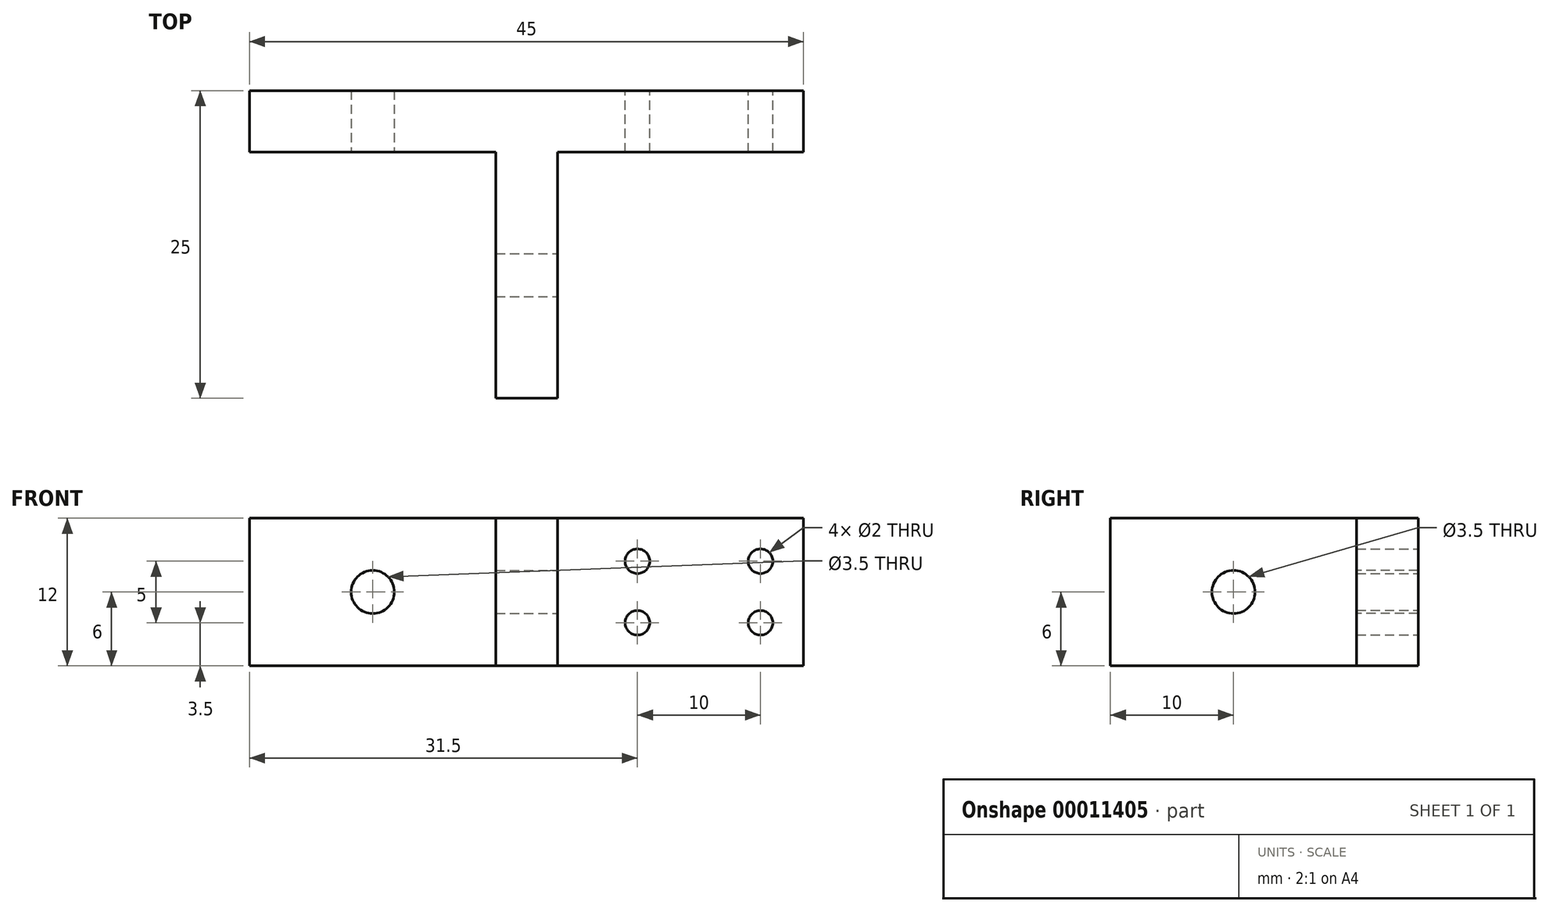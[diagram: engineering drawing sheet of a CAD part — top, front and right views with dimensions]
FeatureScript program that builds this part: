
annotation { "Feature Type Name" : "Feature", "Feature Type Description" : "" }
export const myFeature = defineFeature(function(context is Context, id is Id, definition is map)
    precondition{}
    {
        {
            var Q0;
            Q0=qCreatedBy(makeId("Top.planeOp"),FACE);
            var sketch = newSketch(context, id + "F0", { "sketchPlane" : qUnion([Q0])});
            skLineSegment(sketch, "E0.bottom", {"start": v(20, 0) * mm, "end": v(25, 0) * mm});
            skLineSegment(sketch, "E0.top", {"start": v(0, 25) * mm, "end": v(25, 25) * mm});
            skLineSegment(sketch, "E0.left", {"start": v(0, 20) * mm, "end": v(0, 25) * mm});
            skLineSegment(sketch, "E0.right", {"start": v(25, 0) * mm, "end": v(25, 20) * mm});
            skLineSegment(sketch, "E1.top", {"start": v(0, 20) * mm, "end": v(20, 20) * mm});
            skLineSegment(sketch, "E1.right", {"start": v(20, 0) * mm, "end": v(20, 20) * mm});
            skLineSegment(sketch, "E2.bottom", {"start": v(25, 25) * mm, "end": v(45, 25) * mm});
            skLineSegment(sketch, "E2.top", {"start": v(25, 20) * mm, "end": v(45, 20) * mm});
            skLineSegment(sketch, "E2.right", {"start": v(45, 25) * mm, "end": v(45, 20) * mm});
            skSolve(sketch);
        }
        {
            var Q0;
            Q0=makeQuery(id+"F0.imprint","IMPRINT",FACE,{"disambiguationData":[TD([[makeQuery(id+"F0.imprint","IMPRINT",EDGE,{"derivedFrom":sQuery(id+"F0.wireOp",EDGE,"E0.bottom")}),1.0]])]});
            extrude(context, id + "F1", {"entities" : qUnion([Q0]), "depth" : 12 * mm});
        }
        {
            var Q0;
            Q0=makeQuery(id+"F1.opExtrude","SWEPT_FACE",FACE,{"disambiguationData":[OSD([sQuery(id+"F0.wireOp",EDGE,"E0.right")])]});
            var sketch = newSketch(context, id + "F2", { "sketchPlane" : qUnion([Q0])});
            skCircle(sketch, "E3", {"center": v(10, 6) * mm, "radius": 1.75 * mm});
            skPoint(sketch, "E4.orphan", {"position": v(0, 0) * mm});
            skPoint(sketch, "E5.orphan", {"position": v(20, 12) * mm});
            skSolve(sketch);
        }
        {
            var Q0;
            Q0=makeQuery(id+"F2.imprint","IMPRINT",FACE,{"disambiguationData":[TD([[makeQuery(id+"F2.imprint","IMPRINT",EDGE,{"derivedFrom":sQuery(id+"F2.wireOp",EDGE,"E3")}),1.0]])]});
            var Q1;
            Q1=sQuery(id+"F2.wireOp",EDGE,"E3");
            extrude(context, id + "F3", {"entities" : qUnion([Q0]), "operationType" : NewBodyOperationType.REMOVE, "surfaceEntities" : qUnion([Q1]), "oppositeDirection" : true, "depth" : 5 * mm});
        }
        {
            var Q0;
            Q0=makeQuery(id+"F1.opExtrude","SWEPT_FACE",FACE,{"disambiguationData":[OSD([sQuery(id+"F0.wireOp",EDGE,"E1.top")])]});
            var sketch = newSketch(context, id + "F4", { "sketchPlane" : qUnion([Q0])});
            skCircle(sketch, "E6", {"center": v(10, 6) * mm, "radius": 1.75 * mm});
            skPoint(sketch, "E7.orphan", {"position": v(0, 12) * mm});
            skPoint(sketch, "E8.orphan", {"position": v(20, 0) * mm});
            skSolve(sketch);
        }
        {
            var Q0;
            Q0 = qSketchRegion(id + "F4", true);
            extrude(context, id + "F5", {"entities" : qUnion([Q0]), "operationType" : NewBodyOperationType.REMOVE, "oppositeDirection" : true, "depth" : 5 * mm});
        }
        {
            var Q0;
            Q0=makeQuery(id+"F1.opExtrude","SWEPT_FACE",FACE,{"disambiguationData":[OSD([sQuery(id+"F0.wireOp",EDGE,"E0.top"),sQuery(id+"F0.wireOp",EDGE,"E2.bottom")])]});
            var sketch = newSketch(context, id + "F6", { "sketchPlane" : qUnion([Q0])});
            skLineSegment(sketch, "E9.bottom", {"start": v(-45, 0) * mm, "end": v(-41.5, 0) * mm});
            skLineSegment(sketch, "E9.left", {"start": v(-45, 0) * mm, "end": v(-45, 3.5) * mm});
            skLineSegment(sketch, "E10.bottom", {"start": v(-45, 12) * mm, "end": v(-41.5, 12) * mm});
            skLineSegment(sketch, "E10.left", {"start": v(-45, 12) * mm, "end": v(-45, 8.5) * mm});
            skLineSegment(sketch, "E11.bottom", {"start": v(-41.5, 0) * mm, "end": v(-31.5, 0) * mm});
            skLineSegment(sketch, "E12.bottom", {"start": v(-41.5, 12) * mm, "end": v(-31.5, 12) * mm});
            skCircle(sketch, "E13", {"center": v(-41.5, 3.5) * mm, "radius": 1 * mm});
            skCircle(sketch, "E14", {"center": v(-31.5, 3.5) * mm, "radius": 1 * mm});
            skCircle(sketch, "E15", {"center": v(-31.5, 8.5) * mm, "radius": 1 * mm});
            skCircle(sketch, "E16", {"center": v(-41.5, 8.5) * mm, "radius": 1 * mm});
            skSolve(sketch);
        }
        {
            var Q0;
            Q0=makeQuery(id+"F6.imprint","IMPRINT",FACE,{"disambiguationData":[TD([[makeQuery(id+"F6.imprint","IMPRINT",EDGE,{"derivedFrom":sQuery(id+"F6.wireOp",EDGE,"E16")}),1.0]])]});
            var Q1;
            Q1=makeQuery(id+"F6.imprint","IMPRINT",FACE,{"disambiguationData":[TD([[makeQuery(id+"F6.imprint","IMPRINT",EDGE,{"derivedFrom":sQuery(id+"F6.wireOp",EDGE,"E15")}),1.0]])]});
            var Q2;
            Q2=makeQuery(id+"F6.imprint","IMPRINT",FACE,{"disambiguationData":[TD([[makeQuery(id+"F6.imprint","IMPRINT",EDGE,{"derivedFrom":sQuery(id+"F6.wireOp",EDGE,"E14")}),1.0]])]});
            var Q3;
            Q3=makeQuery(id+"F6.imprint","IMPRINT",FACE,{"disambiguationData":[TD([[makeQuery(id+"F6.imprint","IMPRINT",EDGE,{"derivedFrom":sQuery(id+"F6.wireOp",EDGE,"E13")}),1.0]])]});
            extrude(context, id + "F7", {"entities" : qUnion([Q0, Q1, Q2, Q3]), "operationType" : NewBodyOperationType.REMOVE, "oppositeDirection" : true, "depth" : 5 * mm});
        }
    });
